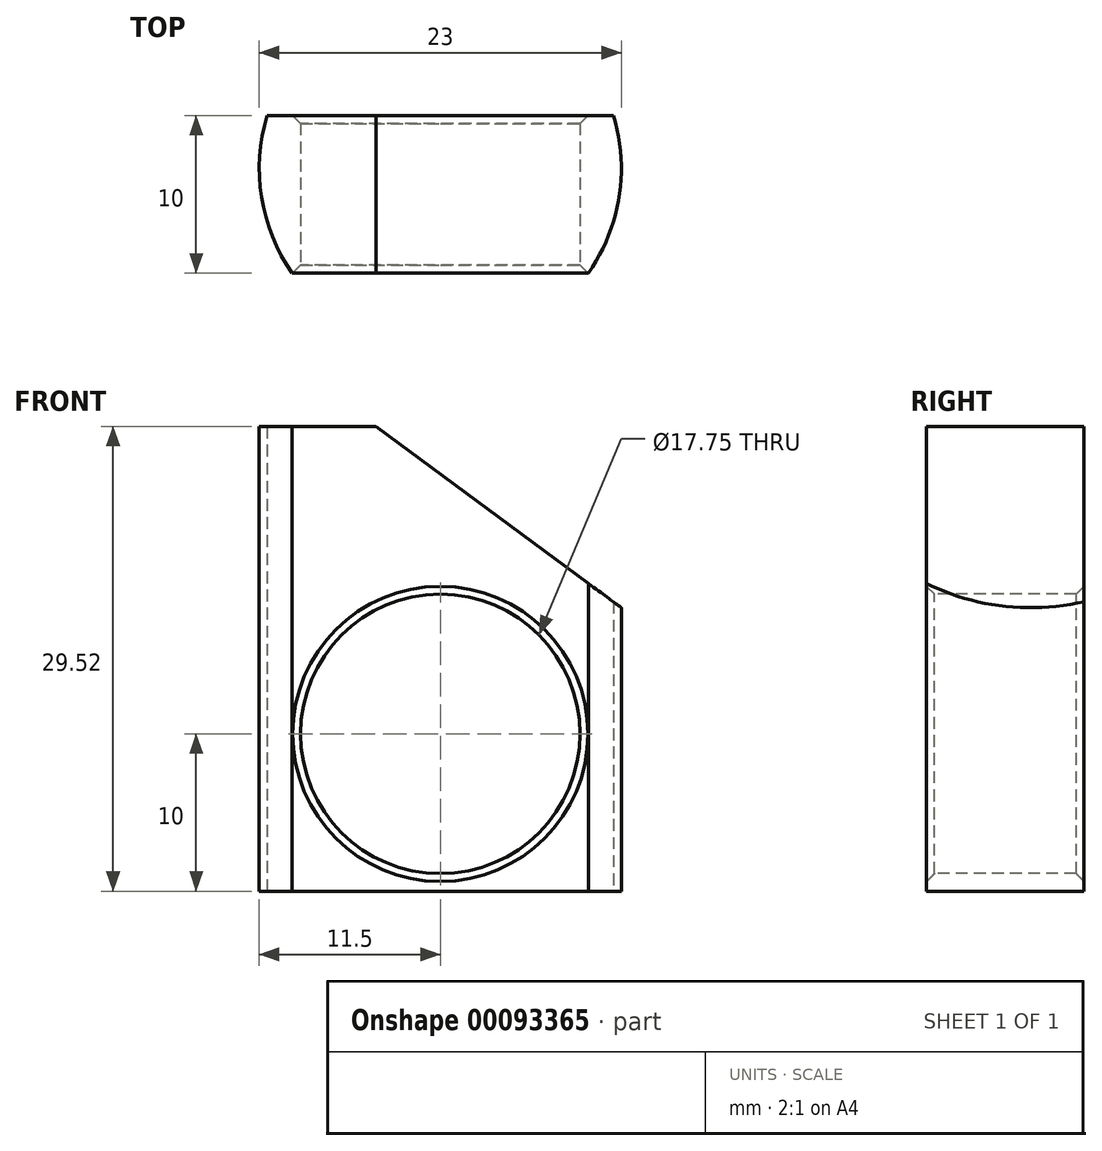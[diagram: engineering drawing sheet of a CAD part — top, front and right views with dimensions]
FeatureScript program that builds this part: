
annotation { "Feature Type Name" : "Feature", "Feature Type Description" : "" }
export const myFeature = defineFeature(function(context is Context, id is Id, definition is map)
    precondition{}
    {
        {
            var Q0;
            Q0=qCreatedBy(makeId("Front.planeOp"),FACE);
            var sketch = newSketch(context, id + "F0", { "sketchPlane" : qUnion([Q0])});
            skCircle(sketch, "E0", {"center": v(0, 0) * mm, "radius": 8.88 * mm});
            skSolve(sketch);
        }
        {
            var Q0;
            Q0=qCreatedBy(makeId("Top.planeOp"),FACE);
            var sketch = newSketch(context, id + "F1", { "sketchPlane" : qUnion([Q0])});
            skCircle(sketch, "E1", {"center": v(0, 0) * mm, "radius": 11.5 * mm});
            skSolve(sketch);
        }
        {
            var Q0;
            Q0=qSketchRegion(id+"F1",true);
            extrude(context, id + "F2", {"entities" : qUnion([Q0]), "depth" : 19.52 * mm, "hasSecondDirection" : true, "secondDirectionOppositeDirection" : true, "secondDirectionDepth" : 10 * mm});
        }
        {
            var Q0;
            Q0=qSketchRegion(id+"F0",true);
            extrude(context, id + "F3", {"entities" : qUnion([Q0]), "operationType" : NewBodyOperationType.REMOVE, "oppositeDirection" : true, "depth" : 25 * mm, "hasSecondDirection" : true, "secondDirectionOppositeDirection" : false, "secondDirectionDepth" : 25 * mm});
        }
        {
            var Q0;
            Q0=qCreatedBy(makeId("Front.planeOp"),FACE);
            var sketch = newSketch(context, id + "F4", { "sketchPlane" : qUnion([Q0])});
            skLineSegment(sketch, "E2", {"start": v(-16.33, 28.55) * mm, "end": v(24.77, -1.78) * mm});
            skLineSegment(sketch, "E3", {"start": v(24.77, -1.78) * mm, "end": v(24.77, 28.55) * mm});
            skLineSegment(sketch, "E4", {"start": v(24.77, 28.55) * mm, "end": v(-16.33, 28.55) * mm});
            skSolve(sketch);
        }
        {
            var Q0;
            Q0=qSketchRegion(id+"F4",true);
            extrude(context, id + "F5", {"entities" : qUnion([Q0]), "operationType" : NewBodyOperationType.REMOVE, "oppositeDirection" : true, "depth" : 25 * mm, "hasSecondDirection" : true, "secondDirectionOppositeDirection" : false, "secondDirectionDepth" : 25 * mm});
        }
        {
            var Q0;
            Q0=qCreatedBy(makeId("Top.planeOp"),FACE);
            var sketch = newSketch(context, id + "F6", { "sketchPlane" : qUnion([Q0])});
            skLineSegment(sketch, "E5.bottom", {"start": v(-13.62, -6.62) * mm, "end": v(17.44, -6.62) * mm});
            skLineSegment(sketch, "E5.top", {"start": v(-13.62, 3.38) * mm, "end": v(17.44, 3.38) * mm});
            skLineSegment(sketch, "E5.left", {"start": v(-13.62, -6.62) * mm, "end": v(-13.62, 3.38) * mm});
            skLineSegment(sketch, "E5.right", {"start": v(17.44, -6.62) * mm, "end": v(17.44, 3.38) * mm});
            skLineSegment(sketch, "E6", {"start": v(-13.62, 3.38) * mm, "end": v(-13.62, 17.25) * mm});
            skLineSegment(sketch, "E7", {"start": v(-13.62, 17.25) * mm, "end": v(17.44, 17.25) * mm});
            skLineSegment(sketch, "E8", {"start": v(17.44, 17.25) * mm, "end": v(17.44, 3.38) * mm});
            skLineSegment(sketch, "E9", {"start": v(-13.62, -6.62) * mm, "end": v(-13.62, -19.8) * mm});
            skLineSegment(sketch, "E10", {"start": v(-13.62, -19.8) * mm, "end": v(17.44, -19.8) * mm});
            skLineSegment(sketch, "E11", {"start": v(17.44, -19.8) * mm, "end": v(17.44, -6.62) * mm});
            skSolve(sketch);
        }
        {
            var Q0;
            Q0=makeQuery(id+"F6.imprint","IMPRINT",FACE,{"disambiguationData":[TD([[makeQuery(id+"F6.imprint","IMPRINT",EDGE,{"derivedFrom":sQuery(id+"F6.wireOp",EDGE,"E5.top")}),1.0]])]});
            var Q1;
            Q1=makeQuery(id+"F6.imprint","IMPRINT",FACE,{"disambiguationData":[TD([[makeQuery(id+"F6.imprint","IMPRINT",EDGE,{"derivedFrom":sQuery(id+"F6.wireOp",EDGE,"E5.bottom")}),-1.0]])]});
            extrude(context, id + "F7", {"entities" : qUnion([Q0, Q1]), "operationType" : NewBodyOperationType.REMOVE, "oppositeDirection" : true, "depth" : 25 * mm, "hasSecondDirection" : true, "secondDirectionOppositeDirection" : false, "secondDirectionDepth" : 25 * mm});
        }
        {
            var Q0;
            Q0=makeQuery(id+"F7.boolean.opBoolean","INTERSECT",EDGE,{"derivedFrom":[makeQuery(id+"F3.boolean.opBoolean","COPY",FACE,{"derivedFrom":makeQuery(id+"F3.opExtrude","SWEPT_FACE",FACE,{"disambiguationData":[OSD([sQuery(id+"F0.wireOp",EDGE,"E0")])]})}),makeQuery(id+"F7.opExtrude","SWEPT_FACE",FACE,{"disambiguationData":[OSD([sQuery(id+"F6.wireOp",EDGE,"E5.top")])]})]});
            var Q1;
            Q1=makeQuery(id+"F7.boolean.opBoolean","INTERSECT",EDGE,{"derivedFrom":[makeQuery(id+"F3.boolean.opBoolean","COPY",FACE,{"derivedFrom":makeQuery(id+"F3.opExtrude","SWEPT_FACE",FACE,{"disambiguationData":[OSD([sQuery(id+"F0.wireOp",EDGE,"E0")])]})}),makeQuery(id+"F7.opExtrude","SWEPT_FACE",FACE,{"disambiguationData":[OSD([sQuery(id+"F6.wireOp",EDGE,"E5.bottom")])]})]});
            chamfer(context, id + "F8", {"entities" : qUnion([Q0, Q1]), "width" : .5 * mm, "tangentPropagation" : true});
        }
    });
